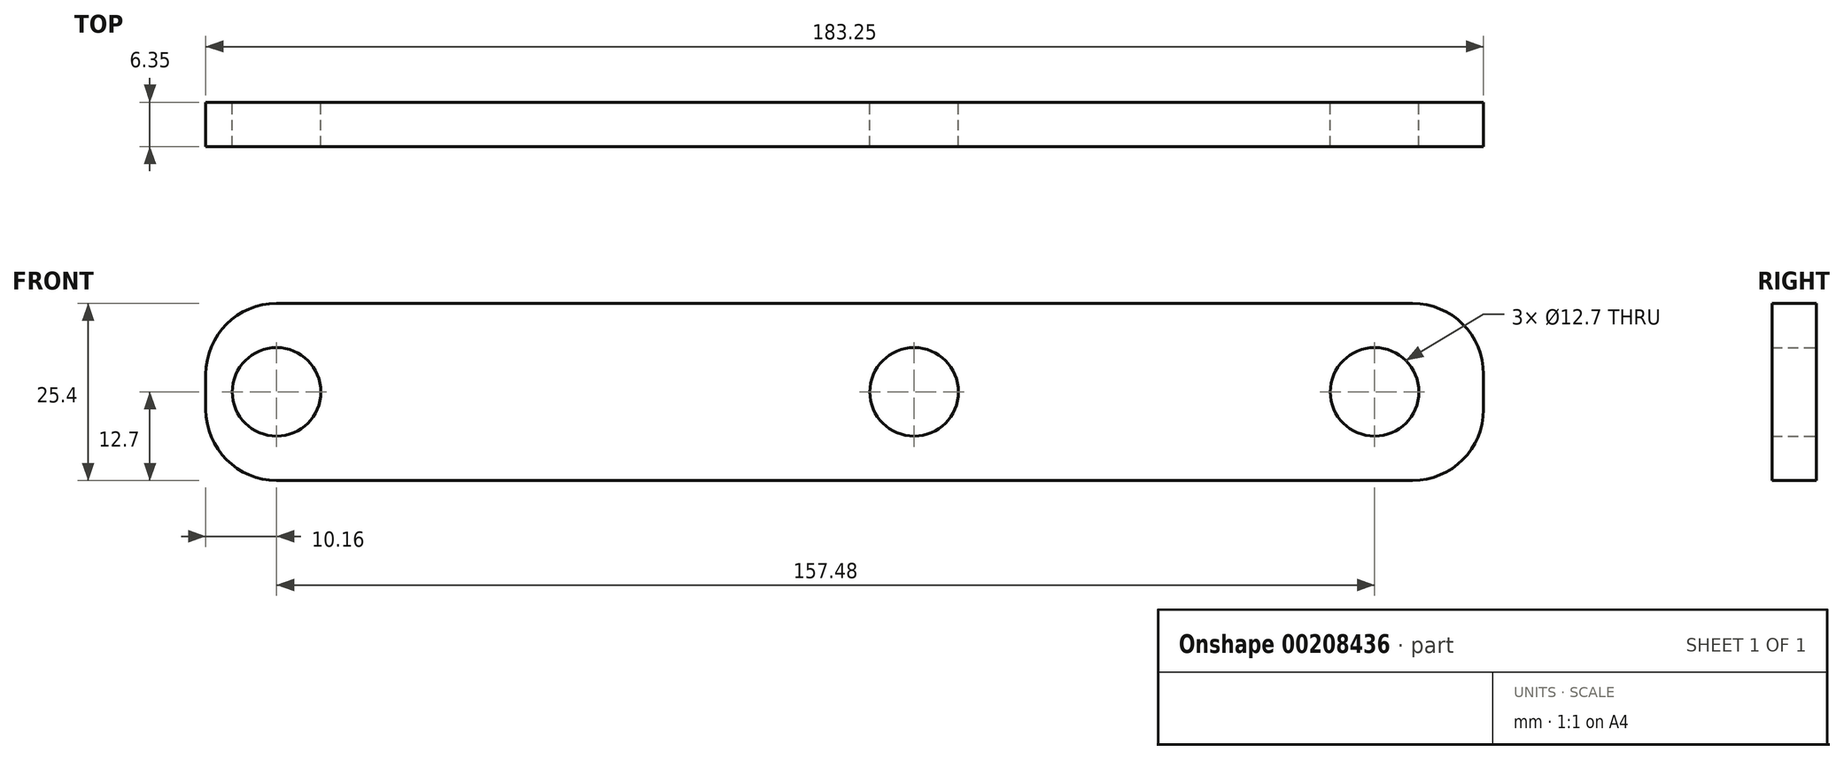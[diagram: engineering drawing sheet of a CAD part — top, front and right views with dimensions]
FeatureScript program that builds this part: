
annotation { "Feature Type Name" : "Feature", "Feature Type Description" : "" }
export const myFeature = defineFeature(function(context is Context, id is Id, definition is map)
    precondition{}
    {
        {
            var Q0;
            Q0=qCreatedBy(makeId("Front.planeOp"),FACE);
            var sketch = newSketch(context, id + "F0", { "sketchPlane" : qUnion([Q0])});
            skLineSegment(sketch, "E0.bottom", {"start": v(71.5, 12.7) * mm, "end": v(-91.44, 12.7) * mm});
            skLineSegment(sketch, "E0.top", {"start": v(71.5, -12.7) * mm, "end": v(-91.44, -12.7) * mm});
            skLineSegment(sketch, "E0.right", {"start": v(-101.6, 2.54) * mm, "end": v(-101.6, -2.54) * mm});
            skPoint(sketch, "E0.middle", {"position": v(0, 0) * mm});
            skPoint(sketch, "E1.visualSharp", {"position": v(-101.6, 12.7) * mm});
            skArc(sketch, "E1.filletArc", {"start": v(-91.44, 12.7) * mm, "mid": v(-98.62, 9.72) * mm, "end": v(-101.6, 2.54) * mm});
            skPoint(sketch, "E2.visualSharp", {"position": v(-101.6, -12.7) * mm});
            skArc(sketch, "E2.filletArc", {"start": v(-101.6, -2.54) * mm, "mid": v(-98.62, -9.72) * mm, "end": v(-91.44, -12.7) * mm});
            skPoint(sketch, "E3.visualSharp", {"position": v(101.6, 12.7) * mm});
            skPoint(sketch, "E4.visualSharp", {"position": v(101.6, -12.7) * mm});
            skCircle(sketch, "E5", {"center": v(-91.44, 0) * mm, "radius": 6.35 * mm});
            skCircle(sketch, "E6", {"center": v(0, 0) * mm, "radius": 6.35 * mm});
            skPoint(sketch, "E7.center.orphan", {"position": v(91.44, 0) * mm});
            skCircle(sketch, "E8", {"center": v(66.04, 0) * mm, "radius": 6.35 * mm});
            skLineSegment(sketch, "E9", {"start": v(81.65, 2.54) * mm, "end": v(81.65, -2.54) * mm});
            skPoint(sketch, "E10.orphan", {"position": v(91.44, 12.7) * mm});
            skPoint(sketch, "E11.orphan", {"position": v(91.44, -12.7) * mm});
            skPoint(sketch, "E12.visualSharp", {"position": v(81.65, 12.7) * mm});
            skArc(sketch, "E12.filletArc", {"start": v(81.65, 2.54) * mm, "mid": v(78.67, 9.72) * mm, "end": v(71.5, 12.7) * mm});
            skPoint(sketch, "E13.visualSharp", {"position": v(81.65, -12.7) * mm});
            skArc(sketch, "E13.filletArc", {"start": v(71.5, -12.7) * mm, "mid": v(78.67, -9.72) * mm, "end": v(81.65, -2.54) * mm});
            skSolve(sketch);
        }
        {
            var Q0;
            Q0=qSketchRegion(id+"F0",true);
            extrude(context, id + "F1", {"entities" : qUnion([Q0]), "depth" : 6.35 * mm});
        }
    });
